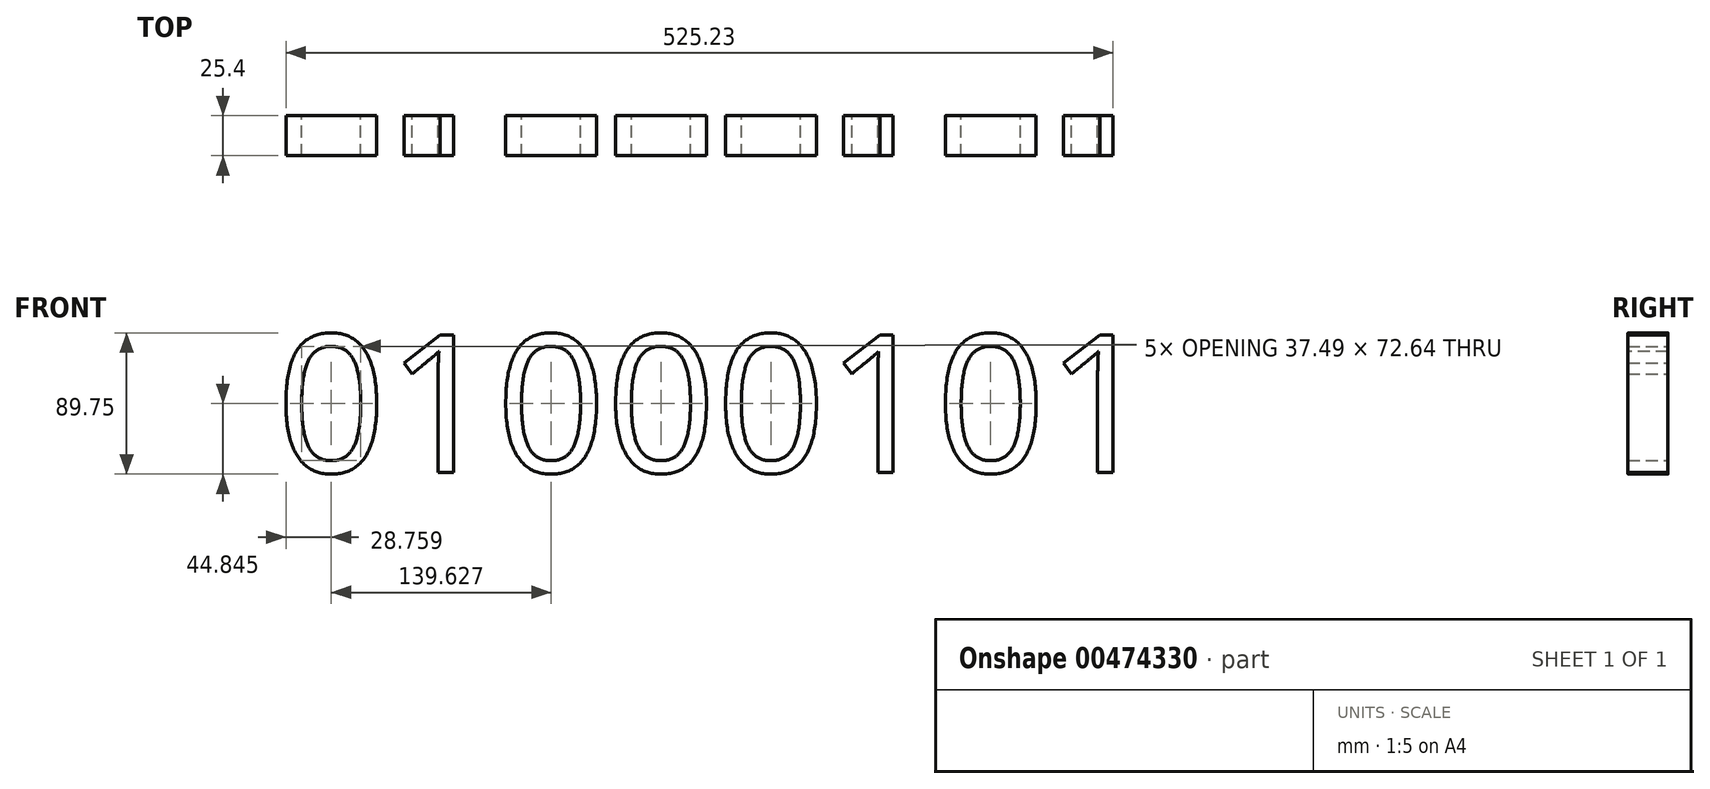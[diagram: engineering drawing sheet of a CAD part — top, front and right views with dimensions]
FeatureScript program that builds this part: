
annotation { "Feature Type Name" : "Feature", "Feature Type Description" : "" }
export const myFeature = defineFeature(function(context is Context, id is Id, definition is map)
    precondition{}
    {
        {
            var Q0;
            Q0=qCreatedBy(makeId("Front.planeOp"),FACE);
            var sketch = newSketch(context, id + "F0", { "sketchPlane" : qUnion([Q0])});
            skText(sketch, "E0", { "text": "01000101", "fontName": "OpenSans-Regular.ttf"});
            const initialGuessF0  = {"E0": [-0.0767, -0.03178, 1, 0, 0.08792]};
            skSetInitialGuess(sketch, initialGuessF0);
            skSolve(sketch);
        }
        {
            var Q0;
            Q0 = qSketchRegion(id + "F0", true);
            extrude(context, id + "F1", {"entities" : qUnion([Q0]), "depth" : 25.4 * mm});
        }
    });
